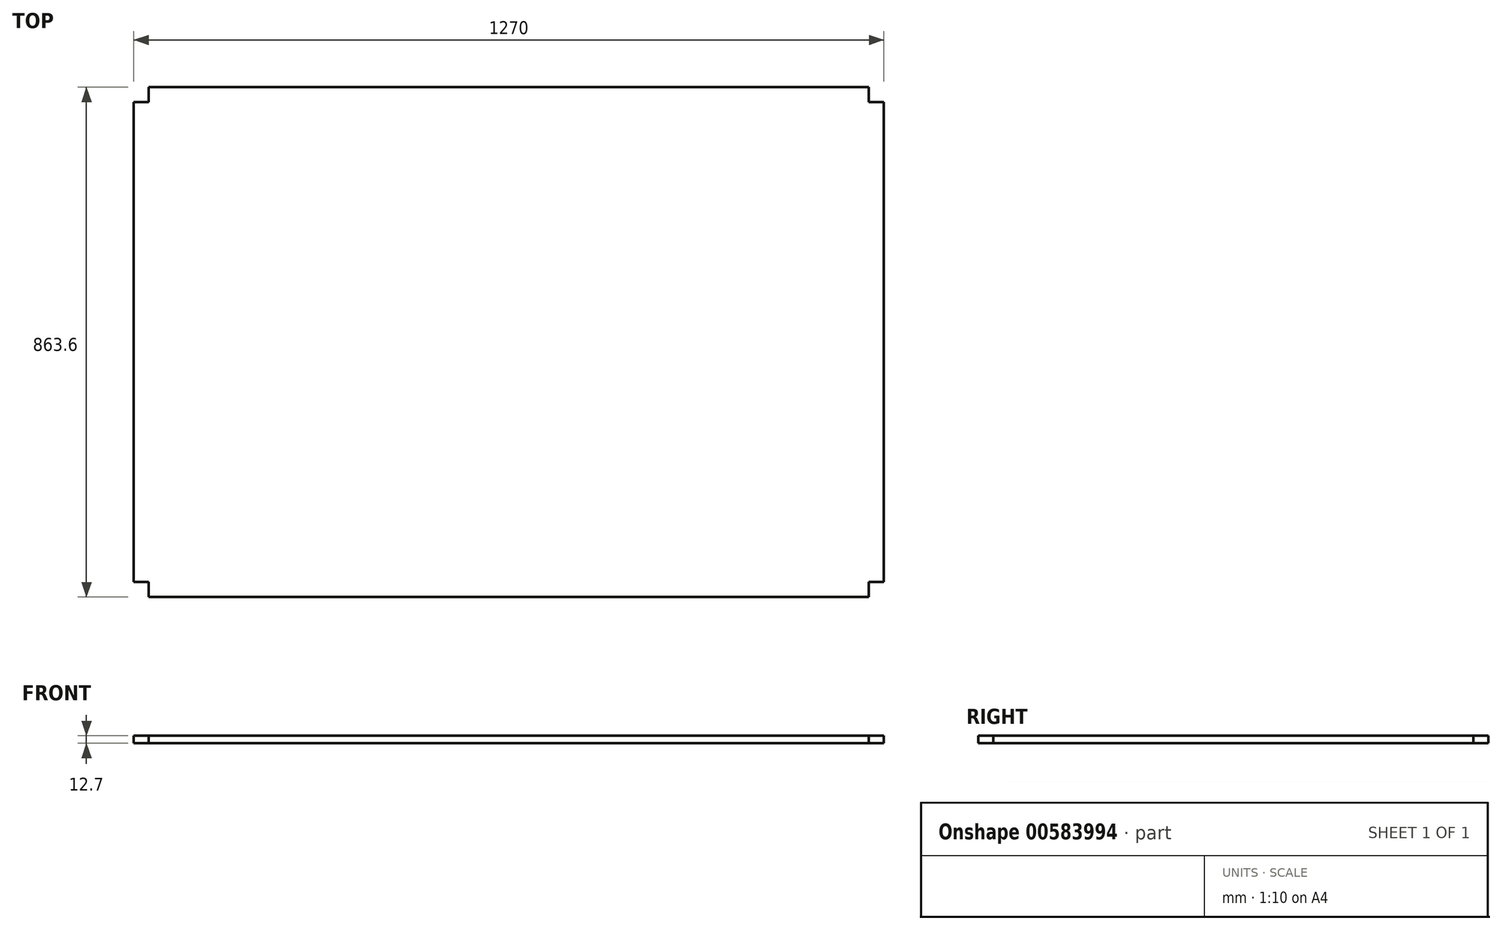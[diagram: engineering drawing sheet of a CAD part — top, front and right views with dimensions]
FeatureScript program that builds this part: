
annotation { "Feature Type Name" : "Feature", "Feature Type Description" : "" }
export const myFeature = defineFeature(function(context is Context, id is Id, definition is map)
    precondition{}
    {
        {
            var Q0;
            Q0=qCreatedBy(makeId("Top.planeOp"),FACE);
            var sketch = newSketch(context, id + "F0", { "sketchPlane" : qUnion([Q0])});
            skLineSegment(sketch, "E0", {"start": v(635, 0) * mm, "end": v(635, 406.4) * mm});
            skLineSegment(sketch, "E1", {"start": v(635, 406.4) * mm, "end": v(609.6, 406.4) * mm});
            skLineSegment(sketch, "E2", {"start": v(609.6, 406.4) * mm, "end": v(609.6, 431.8) * mm});
            skLineSegment(sketch, "E3", {"start": v(609.6, 431.8) * mm, "end": v(0, 431.8) * mm});
            skLineSegment(sketch, "E4", {"start": v(0, 0) * mm, "end": v(0, 1510.56) * mm, "construction": true});
            skLineSegment(sketch, "E5", {"start": v(0, 0) * mm, "end": v(2053.8, 0) * mm, "construction": true});
            skLineSegment(sketch, "E6.MirrorCS", {"start": v(-609.6, 431.8) * mm, "end": v(0, 431.8) * mm});
            skLineSegment(sketch, "E7.MirrorCS", {"start": v(-609.6, 406.4) * mm, "end": v(-609.6, 431.8) * mm});
            skLineSegment(sketch, "E8.MirrorCS", {"start": v(-635, 406.4) * mm, "end": v(-609.6, 406.4) * mm});
            skLineSegment(sketch, "E9.MirrorCS", {"start": v(-635, 0) * mm, "end": v(-635, 406.4) * mm});
            skLineSegment(sketch, "E10.MirrorCS", {"start": v(635, -406.4) * mm, "end": v(609.6, -406.4) * mm});
            skLineSegment(sketch, "E11.MirrorCS", {"start": v(609.6, -406.4) * mm, "end": v(609.6, -431.8) * mm});
            skLineSegment(sketch, "E12.MirrorCS", {"start": v(-609.6, -406.4) * mm, "end": v(-609.6, -431.8) * mm});
            skLineSegment(sketch, "E13.MirrorCS", {"start": v(-635, -406.4) * mm, "end": v(-609.6, -406.4) * mm});
            skLineSegment(sketch, "E14.MirrorCS", {"start": v(635, 0) * mm, "end": v(635, -406.4) * mm});
            skLineSegment(sketch, "E15.MirrorCS", {"start": v(-635, 0) * mm, "end": v(-635, -406.4) * mm});
            skLineSegment(sketch, "E16.MirrorCS", {"start": v(-609.6, -431.8) * mm, "end": v(0, -431.8) * mm});
            skLineSegment(sketch, "E17.MirrorCS", {"start": v(609.6, -431.8) * mm, "end": v(0, -431.8) * mm});
            skLineSegment(sketch, "E18.MirrorCS", {"start": v(0, 0) * mm, "end": v(0, -1510.56) * mm, "construction": true});
            skSolve(sketch);
        }
        {
            var Q0;
            Q0=makeQuery(id+"F0.imprint","IMPRINT",FACE,{"disambiguationData":[TD([[makeQuery(id+"F0.imprint","IMPRINT",EDGE,{"derivedFrom":sQuery(id+"F0.wireOp",EDGE,"E0")}),1.0]])]});
            extrude(context, id + "F1", {"entities" : qUnion([Q0]), "depth" : 12.7 * mm, "offsetDistance" : 25.4 * mm});
        }
    });
